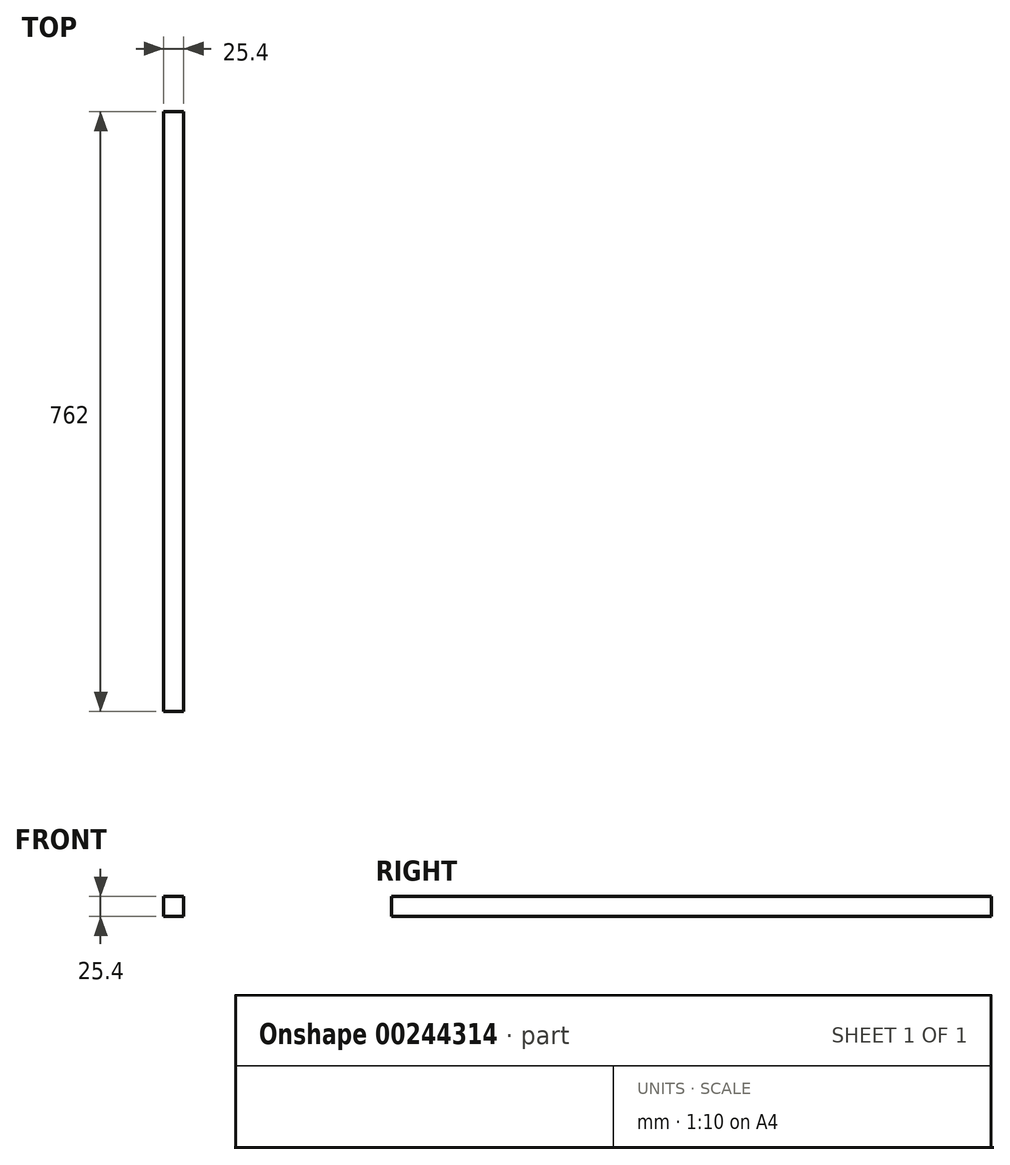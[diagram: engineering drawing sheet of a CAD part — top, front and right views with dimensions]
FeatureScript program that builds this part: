
annotation { "Feature Type Name" : "Feature", "Feature Type Description" : "" }
export const myFeature = defineFeature(function(context is Context, id is Id, definition is map)
    precondition{}
    {
        {
            var Q0;
            Q0=qCreatedBy(makeId("Right.planeOp"),FACE);
            var sketch = newSketch(context, id + "F0", { "sketchPlane" : qUnion([Q0])});
            skLineSegment(sketch, "E0", {"start": v(-282.3, 0) * mm, "end": v(479.7, 0) * mm});
            skLineSegment(sketch, "E1", {"start": v(-282.3, 0) * mm, "end": v(-282.3, -25.4) * mm});
            skLineSegment(sketch, "E2", {"start": v(479.7, 0) * mm, "end": v(479.7, -25.4) * mm});
            skLineSegment(sketch, "E3", {"start": v(-282.3, -25.4) * mm, "end": v(479.7, -25.4) * mm});
            skSolve(sketch);
        }
        {
            var Q0;
            Q0=makeQuery(id+"F0.imprint","IMPRINT",FACE,{"disambiguationData":[TD([[makeQuery(id+"F0.imprint","IMPRINT",EDGE,{"derivedFrom":sQuery(id+"F0.wireOp",EDGE,"E0")}),-1.0]])]});
            extrude(context, id + "F1", {"entities" : qUnion([Q0]), "depth" : 25.4 * mm});
        }
    });
